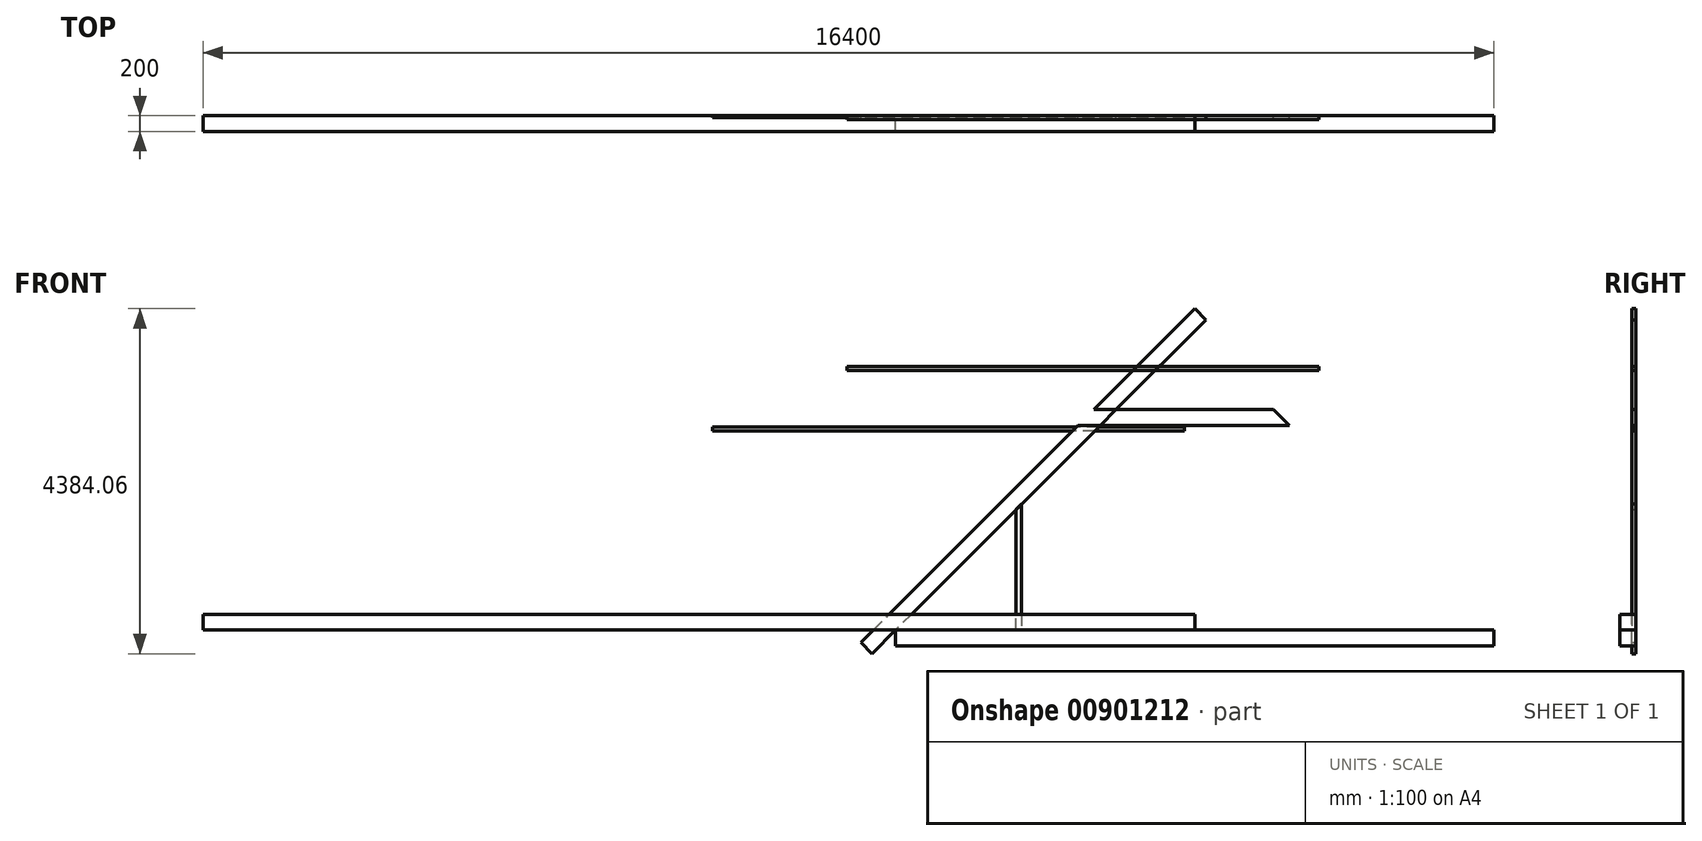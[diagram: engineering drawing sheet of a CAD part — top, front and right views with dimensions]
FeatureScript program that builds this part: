
annotation { "Feature Type Name" : "Feature", "Feature Type Description" : "" }
export const myFeature = defineFeature(function(context is Context, id is Id, definition is map)
    precondition{}
    {
        {
            var Q0;
            Q0=qCreatedBy(makeId("Front.planeOp"),FACE);
            var sketch = newSketch(context, id + "F0", { "sketchPlane" : qUnion([Q0])});
            skLineSegment(sketch, "E0", {"start": v(-3800, 0) * mm, "end": v(3800, 0) * mm});
            skLineSegment(sketch, "E1", {"start": v(0, 0) * mm, "end": v(0, 3800) * mm, "construction": true});
            skLineSegment(sketch, "E2", {"start": v(0, 3800) * mm, "end": v(-4101.22, -301.22) * mm});
            skLineSegment(sketch, "E3", {"start": v(0, 3800) * mm, "end": v(4101.22, -301.22) * mm});
            skLineSegment(sketch, "E4", {"start": v(-4101.22, -301.22) * mm, "end": v(-4242.64, -159.8) * mm});
            skLineSegment(sketch, "E5", {"start": v(-4242.64, -159.8) * mm, "end": v(-141.42, 3941.42) * mm});
            skLineSegment(sketch, "E6", {"start": v(-141.42, 3941.42) * mm, "end": v(0, 3800) * mm, "construction": true});
            skLineSegment(sketch, "E7", {"start": v(0, 3800) * mm, "end": v(141.42, 3941.42) * mm, "construction": true});
            skLineSegment(sketch, "E8", {"start": v(4101.22, -301.22) * mm, "end": v(4242.64, -159.8) * mm});
            skLineSegment(sketch, "E9", {"start": v(4242.64, -159.8) * mm, "end": v(141.42, 3941.42) * mm});
            skLineSegment(sketch, "E10", {"start": v(-141.42, 3941.42) * mm, "end": v(0, 4082.84) * mm});
            skLineSegment(sketch, "E11", {"start": v(0, 3800) * mm, "end": v(141.42, 3941.42) * mm});
            skLineSegment(sketch, "E12", {"start": v(141.42, 3941.42) * mm, "end": v(0, 4082.84) * mm});
            skLineSegment(sketch, "E13", {"start": v(0, 4082.84) * mm, "end": v(-141.42, 3941.42) * mm});
            skLineSegment(sketch, "E14", {"start": v(-141.42, 3941.42) * mm, "end": v(0, 3800) * mm});
            skLineSegment(sketch, "E15.bottom", {"start": v(-1282.84, 2800) * mm, "end": v(1282.84, 2800) * mm});
            skLineSegment(sketch, "E15.top", {"start": v(-1482.84, 2600) * mm, "end": v(1482.84, 2600) * mm});
            skLineSegment(sketch, "E16", {"start": v(-1482.84, 2600) * mm, "end": v(-1282.84, 2800) * mm});
            skLineSegment(sketch, "E17", {"start": v(1482.84, 2600) * mm, "end": v(1282.84, 2800) * mm});
            skLineSegment(sketch, "E18", {"start": v(-2200, 1600) * mm, "end": v(-2200, 0) * mm});
            skLineSegment(sketch, "E19", {"start": v(2200, 1600) * mm, "end": v(2200, 0) * mm});
            skLineSegment(sketch, "E20", {"start": v(-3800, 0) * mm, "end": v(-3800, -200) * mm});
            skLineSegment(sketch, "E21", {"start": v(-3800, -200) * mm, "end": v(3800, -200) * mm});
            skLineSegment(sketch, "E22", {"start": v(3800, -200) * mm, "end": v(3800, 0) * mm});
            skLineSegment(sketch, "E23", {"start": v(-2200, 0) * mm, "end": v(-2270, 0) * mm});
            skLineSegment(sketch, "E24", {"start": v(-2270, 0) * mm, "end": v(-2270, 1530) * mm});
            skLineSegment(sketch, "E25", {"start": v(-2270, 1530) * mm, "end": v(-2200, 1600) * mm});
            skLineSegment(sketch, "E26", {"start": v(2200, 0) * mm, "end": v(2270, 0) * mm});
            skLineSegment(sketch, "E27", {"start": v(2270, 0) * mm, "end": v(2270, 1530) * mm});
            skLineSegment(sketch, "E28", {"start": v(2270, 1530) * mm, "end": v(2200, 1600) * mm});
            skSolve(sketch);
        }
        {
            var Q0;
            {var subQ0=sQuery(id+"F0.wireOp",EDGE,"E20");Q0=makeQuery(id+"F0.imprint","IMPRINT",FACE,{"disambiguationData":[TD([[makeQuery(id+"F0.imprint","IMPRINT",EDGE,{"derivedFrom":subQ0}),1.0]])]});}
            extrude(context, id + "F1", {"entities" : qUnion([Q0]), "depth" : 200 * mm, "offsetDistance" : 25 * mm});
        }
        {
            var Q0;
            Q0=makeQuery(id+"F0.imprint","IMPRINT",FACE,{"disambiguationData":[TD([[makeQuery(id+"F0.imprint","IMPRINT",EDGE,{"derivedFrom":sQuery(id+"F0.wireOp",EDGE,"E18")}),-1.0]])]});
            extrude(context, id + "F2", {"entities" : qUnion([Q0]), "depth" : 50 * mm, "offsetDistance" : 25 * mm});
        }
        {
            var Q0;
            {var subQ5=sQuery(id+"F0.wireOp",EDGE,"E16");Q0=makeQuery(id+"F0.imprint","IMPRINT",FACE,{"disambiguationData":[TD([[makeQuery(id+"F0.imprint","IMPRINT",EDGE,{"derivedFrom":subQ5}),-1.0]])]});}
            var Q1;
            {var subQ0=sQuery(id+"F0.wireOp",EDGE,"E15.bottom");var subQ1=sQuery(id+"F0.wireOp",EDGE,"E2");var subQ2=makeQuery(id+"F0.imprint","INTERSECT",VERTEX,{"derivedFrom":[subQ1,subQ0]});Q1=makeQuery(id+"F0.imprint","IMPRINT",FACE,{"disambiguationData":[TD([[makeQuery(id+"F0.imprint","IMPRINT",EDGE,{"disambiguationData":[TD([[subQ2,-1.0]])],"derivedFrom":subQ1}),1.0]])]});}
            var Q2;
            {var subQ5=sQuery(id+"F0.wireOp",EDGE,"E17");Q2=makeQuery(id+"F0.imprint","IMPRINT",FACE,{"disambiguationData":[TD([[makeQuery(id+"F0.imprint","IMPRINT",EDGE,{"derivedFrom":subQ5}),1.0]])]});}
            extrude(context, id + "F3", {"entities" : qUnion([Q0, Q1, Q2]), "depth" : 50 * mm, "offsetDistance" : 25 * mm});
        }
        {
            var Q0;
            {var subQ0=sQuery(id+"F0.wireOp",EDGE,"E4");Q0=makeQuery(id+"F0.imprint","IMPRINT",FACE,{"disambiguationData":[TD([[makeQuery(id+"F0.imprint","IMPRINT",EDGE,{"derivedFrom":subQ0}),-1.0]])]});}
            var Q1;
            {var subQ5=sQuery(id+"F0.wireOp",EDGE,"E16");Q1=makeQuery(id+"F0.imprint","IMPRINT",FACE,{"disambiguationData":[TD([[makeQuery(id+"F0.imprint","IMPRINT",EDGE,{"derivedFrom":subQ5}),-1.0]])]});}
            var Q2;
            {var subQ0=sQuery(id+"F0.wireOp",EDGE,"E14");Q2=makeQuery(id+"F0.imprint","IMPRINT",FACE,{"disambiguationData":[TD([[makeQuery(id+"F0.imprint","IMPRINT",EDGE,{"derivedFrom":subQ0}),-1.0]])]});}
            var Q3;
            Q3=makeQuery(id+"F0.imprint","IMPRINT",FACE,{"disambiguationData":[TD([[makeQuery(id+"F0.imprint","IMPRINT",EDGE,{"derivedFrom":sQuery(id+"F0.wireOp",EDGE,"E11")}),1.0]])]});
            extrude(context, id + "F4", {"entities" : qUnion([Q0, Q1, Q2, Q3]), "depth" : 50 * mm, "offsetDistance" : 25 * mm});
        }
        {
            var Q0;
            Q0=qCreatedBy(makeId("Front.planeOp"),FACE);
            var sketch = newSketch(context, id + "F5", { "sketchPlane" : qUnion([Q0])});
            skLineSegment(sketch, "E29.bottom", {"start": v(0, 0) * mm, "end": v(-12600, 0) * mm});
            skLineSegment(sketch, "E29.top", {"start": v(0, 200) * mm, "end": v(-12600, 200) * mm});
            skLineSegment(sketch, "E29.left", {"start": v(0, 0) * mm, "end": v(0, 200) * mm});
            skLineSegment(sketch, "E29.right", {"start": v(-12600, 0) * mm, "end": v(-12600, 200) * mm});
            skSolve(sketch);
        }
        {
            var Q0;
            Q0 = qSketchRegion(id + "F5", true);
            extrude(context, id + "F6", {"entities" : qUnion([Q0]), "depth" : 200 * mm, "offsetDistance" : 25 * mm});
        }
        {
            var Q0;
            Q0=qCreatedBy(makeId("Front.planeOp"),FACE);
            var sketch = newSketch(context, id + "F7", { "sketchPlane" : qUnion([Q0])});
            skLineSegment(sketch, "E30.bottom", {"start": v(-129.32, 2527.6) * mm, "end": v(-6129.32, 2527.6) * mm});
            skLineSegment(sketch, "E30.top", {"start": v(-129.32, 2577.6) * mm, "end": v(-6129.32, 2577.6) * mm});
            skLineSegment(sketch, "E30.left", {"start": v(-129.32, 2527.6) * mm, "end": v(-129.32, 2577.6) * mm});
            skLineSegment(sketch, "E30.right", {"start": v(-6129.32, 2527.6) * mm, "end": v(-6129.32, 2577.6) * mm});
            skSolve(sketch);
        }
        {
            var Q0;
            Q0 = qSketchRegion(id + "F7", true);
            extrude(context, id + "F8", {"entities" : qUnion([Q0]), "depth" : 22 * mm, "offsetDistance" : 25 * mm});
        }
        {
            var Q0;
            Q0=qCreatedBy(makeId("Front.planeOp"),FACE);
            var sketch = newSketch(context, id + "F9", { "sketchPlane" : qUnion([Q0])});
            skLineSegment(sketch, "E31.bottom", {"start": v(1578.3, 3296.6) * mm, "end": v(-4421.7, 3296.6) * mm});
            skLineSegment(sketch, "E31.top", {"start": v(1578.3, 3346.6) * mm, "end": v(-4421.7, 3346.6) * mm});
            skLineSegment(sketch, "E31.left", {"start": v(1578.3, 3296.6) * mm, "end": v(1578.3, 3346.6) * mm});
            skLineSegment(sketch, "E31.right", {"start": v(-4421.7, 3296.6) * mm, "end": v(-4421.7, 3346.6) * mm});
            skSolve(sketch);
        }
        {
            var Q0;
            Q0 = qSketchRegion(id + "F9", true);
            extrude(context, id + "F10", {"entities" : qUnion([Q0]), "depth" : 50 * mm, "offsetDistance" : 25 * mm});
        }
    });
